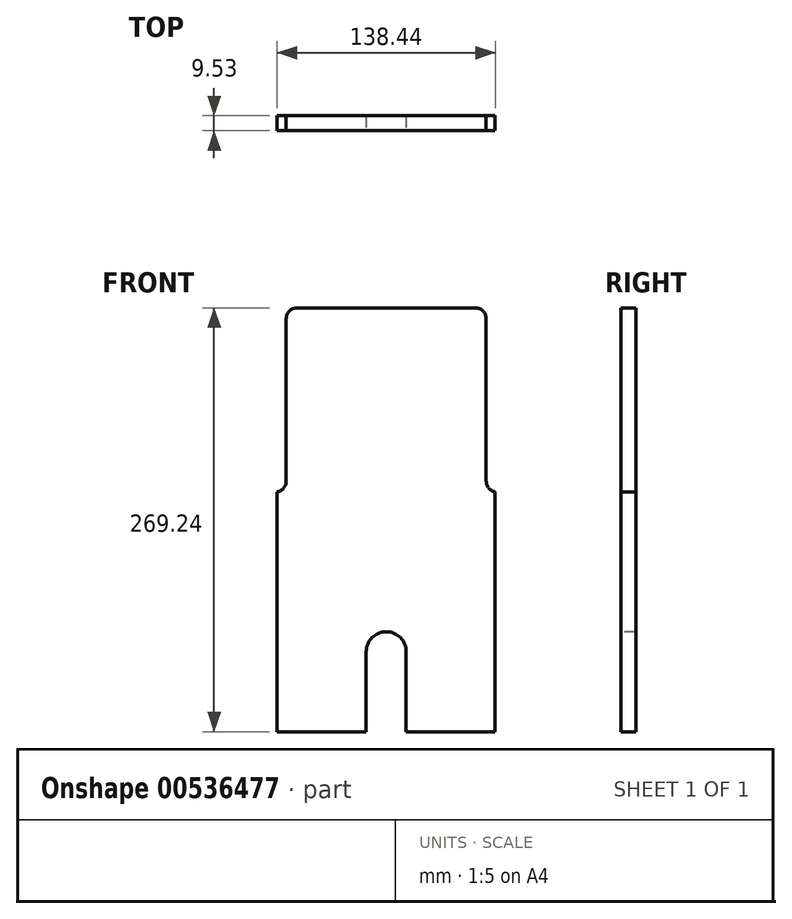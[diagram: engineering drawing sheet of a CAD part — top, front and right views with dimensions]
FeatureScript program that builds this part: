
annotation { "Feature Type Name" : "Feature", "Feature Type Description" : "" }
export const myFeature = defineFeature(function(context is Context, id is Id, definition is map)
    precondition{}
    {
        {
            var Q0;
            Q0=qCreatedBy(makeId("Front.planeOp"),FACE);
            var sketch = newSketch(context, id + "F0", { "sketchPlane" : qUnion([Q0])});
            skLineSegment(sketch, "E0.bottom", {"start": v(0, 0) * mm, "end": v(119.38, 0) * mm});
            skLineSegment(sketch, "E0.left", {"start": v(0, 0) * mm, "end": v(0, 152.4) * mm});
            skLineSegment(sketch, "E0.right", {"start": v(119.38, 0) * mm, "end": v(119.38, 152.4) * mm});
            skLineSegment(sketch, "E1.bottom", {"start": v(3.05, 269.24) * mm, "end": v(116.33, 269.24) * mm});
            skLineSegment(sketch, "E1.left", {"start": v(-3.81, 262.38) * mm, "end": v(-3.81, 158.55) * mm});
            skLineSegment(sketch, "E1.right", {"start": v(123.19, 262.38) * mm, "end": v(123.19, 158.55) * mm});
            skPoint(sketch, "E2.visualSharp", {"position": v(-3.81, 269.24) * mm});
            skArc(sketch, "E2.filletArc", {"start": v(3.05, 269.24) * mm, "mid": v(-1.8, 267.23) * mm, "end": v(-3.81, 262.38) * mm});
            skPoint(sketch, "E3.visualSharp", {"position": v(123.19, 269.24) * mm});
            skArc(sketch, "E3.filletArc", {"start": v(123.19, 262.38) * mm, "mid": v(121.18, 267.23) * mm, "end": v(116.33, 269.24) * mm});
            skPoint(sketch, "E4", {"position": v(-3.81, 158.55) * mm});
            skPoint(sketch, "E5", {"position": v(123.19, 158.55) * mm});
            skArc(sketch, "E6", {"start": v(-3.81, 158.55) * mm, "mid": v(-2.78, 154.93) * mm, "end": v(0, 152.4) * mm});
            skArc(sketch, "E7", {"start": v(123.19, 158.55) * mm, "mid": v(122.16, 154.93) * mm, "end": v(119.38, 152.4) * mm});
            skLineSegment(sketch, "E8", {"start": v(-3.81, 158.55) * mm, "end": v(3.05, 158.55) * mm, "construction": true});
            skLineSegment(sketch, "E9", {"start": v(123.19, 158.55) * mm, "end": v(116.33, 158.55) * mm, "construction": true});
            skLineSegment(sketch, "E10", {"start": v(59.7, 0) * mm, "end": v(59.69, 269.24) * mm, "construction": true});
            skSolve(sketch);
        }
        {
            var Q0;
            Q0 = qSketchRegion(id + "F0", true);
            extrude(context, id + "F1", {"entities" : qUnion([Q0]), "depth" : 9.52 * mm, "offsetDistance" : 25.4 * mm});
        }
        {
            var Q0;
            Q0=makeQuery(id+"F1.opExtrude","CAP_FACE",FACE,{"disambiguationData":[OSD([sQuery(id+"F0.wireOp",EDGE,"E0.bottom"),sQuery(id+"F0.wireOp",EDGE,"E0.top"),sQuery(id+"F0.wireOp",EDGE,"E0.left"),sQuery(id+"F0.wireOp",EDGE,"E0.right")])],"isStart":false});
            var sketch = newSketch(context, id + "F2", { "sketchPlane" : qUnion([Q0])});
            skLineSegment(sketch, "E11.bottom", {"start": v(47, 0) * mm, "end": v(72.4, 0) * mm});
            skLineSegment(sketch, "E11.top", {"start": v(47, 50.8) * mm, "end": v(72.39, 50.8) * mm, "construction": true});
            skLineSegment(sketch, "E11.left", {"start": v(47, 0) * mm, "end": v(47, 50.8) * mm});
            skLineSegment(sketch, "E11.right", {"start": v(72.4, 0) * mm, "end": v(72.4, 50.8) * mm});
            skArc(sketch, "E12", {"start": v(72.39, 50.8) * mm, "mid": v(59.69, 63.5) * mm, "end": v(47, 50.8) * mm});
            skLineSegment(sketch, "E13", {"start": v(59.7, 0) * mm, "end": v(59.69, 50.8) * mm, "construction": true});
            skSolve(sketch);
        }
        {
            var Q0;
            Q0 = qSketchRegion(id + "F2", true);
            extrude(context, id + "F3", {"entities" : qUnion([Q0]), "operationType" : NewBodyOperationType.REMOVE, "oppositeDirection" : true, "depth" : 25.4 * mm, "offsetDistance" : 25.4 * mm});
        }
        {
            var Q0;
            Q0=makeQuery(id+"F1.opExtrude","CAP_FACE",FACE,{"disambiguationData":[OSD([sQuery(id+"F0.wireOp",EDGE,"E0.bottom"),sQuery(id+"F0.wireOp",EDGE,"E0.left"),sQuery(id+"F0.wireOp",EDGE,"E0.right"),sQuery(id+"F0.wireOp",EDGE,"E1.bottom"),sQuery(id+"F0.wireOp",EDGE,"E1.left"),sQuery(id+"F0.wireOp",EDGE,"E1.right"),sQuery(id+"F0.wireOp",EDGE,"E2.filletArc"),sQuery(id+"F0.wireOp",EDGE,"E3.filletArc"),sQuery(id+"F0.wireOp",EDGE,"E6"),sQuery(id+"F0.wireOp",EDGE,"E7")])],"isStart":false});
            var sketch = newSketch(context, id + "F4", { "sketchPlane" : qUnion([Q0])});
            skLineSegment(sketch, "E14.bottom", {"start": v(119.38, 0) * mm, "end": v(128.9, 0) * mm});
            skLineSegment(sketch, "E14.top", {"start": v(119.38, 152.4) * mm, "end": v(128.9, 152.4) * mm});
            skLineSegment(sketch, "E14.left", {"start": v(119.38, 0) * mm, "end": v(119.38, 152.4) * mm});
            skLineSegment(sketch, "E14.right", {"start": v(128.9, 0) * mm, "end": v(128.9, 152.4) * mm});
            skLineSegment(sketch, "E15.bottom", {"start": v(0, 0) * mm, "end": v(-9.53, 0) * mm});
            skLineSegment(sketch, "E15.top", {"start": v(0, 152.4) * mm, "end": v(-9.52, 152.4) * mm});
            skLineSegment(sketch, "E15.left", {"start": v(0, 0) * mm, "end": v(0, 152.4) * mm});
            skLineSegment(sketch, "E15.right", {"start": v(-9.52, 0) * mm, "end": v(-9.52, 152.4) * mm});
            skSolve(sketch);
        }
        {
            var Q0;
            Q0 = qSketchRegion(id + "F4", true);
            extrude(context, id + "F5", {"entities" : qUnion([Q0]), "operationType" : NewBodyOperationType.ADD, "oppositeDirection" : true, "depth" : 9.52 * mm, "offsetDistance" : 25.4 * mm});
        }
        {
            var Q0;
            {var subQ0=sQuery(id+"F0.wireOp",EDGE,"E7");Q0=makeQuery(id+"F5.boolean.opBoolean","MERGE",EDGE,{"derivedFrom":[makeQuery(id+"F1.opExtrude","SWEPT_EDGE",EDGE,{"disambiguationData":[OSD([sQuery(id+"F0.wireOp",EDGE,"E0.right"),subQ0])]}),makeQuery(id+"F5.opExtrude","SWEPT_EDGE",EDGE,{"disambiguationData":[OSD([subQ0,sQuery(id+"F4.wireOp",EDGE,"E14.top"),sQuery(id+"F4.wireOp",EDGE,"E14.left")])]})]});}
            var Q1;
            {var subQ0=sQuery(id+"F0.wireOp",EDGE,"E6");Q1=makeQuery(id+"F5.boolean.opBoolean","MERGE",EDGE,{"derivedFrom":[makeQuery(id+"F1.opExtrude","SWEPT_EDGE",EDGE,{"disambiguationData":[OSD([sQuery(id+"F0.wireOp",EDGE,"E0.left"),subQ0])]}),makeQuery(id+"F5.opExtrude","SWEPT_EDGE",EDGE,{"disambiguationData":[OSD([subQ0,sQuery(id+"F4.wireOp",EDGE,"E15.top"),sQuery(id+"F4.wireOp",EDGE,"E15.left")])]})]});}
            fillet(context, id + "F6", {"entities" : qUnion([Q0, Q1]), "radius" : 6.86 * mm, "tangentPropagation" : true, "allowEdgeOverflow" : false});
        }
    });
